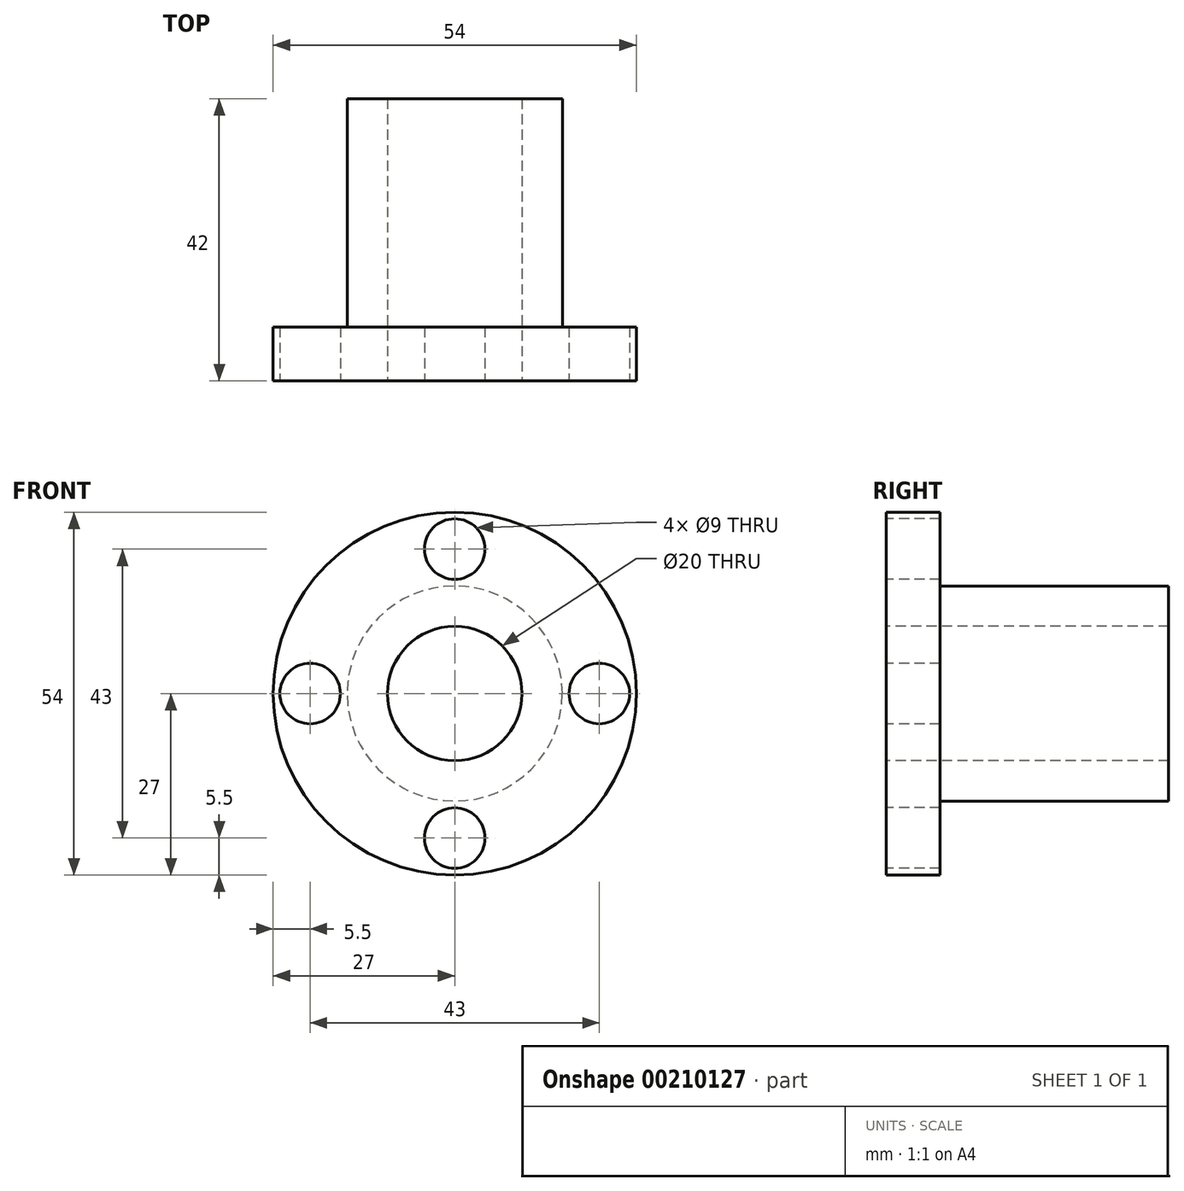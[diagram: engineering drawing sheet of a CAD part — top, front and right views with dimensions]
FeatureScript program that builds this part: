
annotation { "Feature Type Name" : "Feature", "Feature Type Description" : "" }
export const myFeature = defineFeature(function(context is Context, id is Id, definition is map)
    precondition{}
    {
        {
            var Q0;
            Q0=qCreatedBy(makeId("Front.planeOp"),FACE);
            var sketch = newSketch(context, id + "F0", { "sketchPlane" : qUnion([Q0])});
            skCircle(sketch, "E0", {"center": v(0, 0) * mm, "radius": 27 * mm});
            skSolve(sketch);
        }
        {
            var Q0;
            Q0 = qSketchRegion(id + "F0", true);
            extrude(context, id + "F1", {"entities" : qUnion([Q0]), "depth" : 8 * mm});
        }
        {
            var Q0;
            Q0=makeQuery(id+"F1.opExtrude","CAP_FACE",FACE,{"disambiguationData":[OSD([sQuery(id+"F0.wireOp",EDGE,"E0")])],"isStart":true});
            var sketch = newSketch(context, id + "F2", { "sketchPlane" : qUnion([Q0])});
            skCircle(sketch, "E1", {"center": v(0, 0) * mm, "radius": 16 * mm});
            skSolve(sketch);
        }
        {
            var Q0;
            Q0 = qSketchRegion(id + "F2", true);
            extrude(context, id + "F3", {"entities" : qUnion([Q0]), "operationType" : NewBodyOperationType.ADD, "depth" : (42 - 8) * mm});
        }
        {
            var Q0;
            Q0=makeQuery(id+"F1.opExtrude","CAP_FACE",FACE,{"disambiguationData":[OSD([sQuery(id+"F0.wireOp",EDGE,"E0")])],"isStart":false});
            var sketch = newSketch(context, id + "F4", { "sketchPlane" : qUnion([Q0])});
            skCircle(sketch, "E2", {"center": v(0, 0) * mm, "radius": 10 * mm});
            skCircle(sketch, "E3", {"center": v(0, 0) * mm, "radius": 21.5 * mm, "construction": true});
            skCircle(sketch, "E4", {"center": v(0, 21.5) * mm, "radius": 4.5 * mm});
            skCircle(sketch, "E5", {"center": v(-21.5, 0) * mm, "radius": 4.5 * mm});
            skCircle(sketch, "E6", {"center": v(0, -21.5) * mm, "radius": 4.5 * mm});
            skCircle(sketch, "E7", {"center": v(21.5, 0) * mm, "radius": 4.5 * mm});
            skSolve(sketch);
        }
        {
            var Q0;
            Q0 = qSketchRegion(id + "F4", true);
            extrude(context, id + "F5", {"entities" : qUnion([Q0]), "operationType" : NewBodyOperationType.REMOVE, "oppositeDirection" : true, "depth" : 50 * mm});
        }
    });
